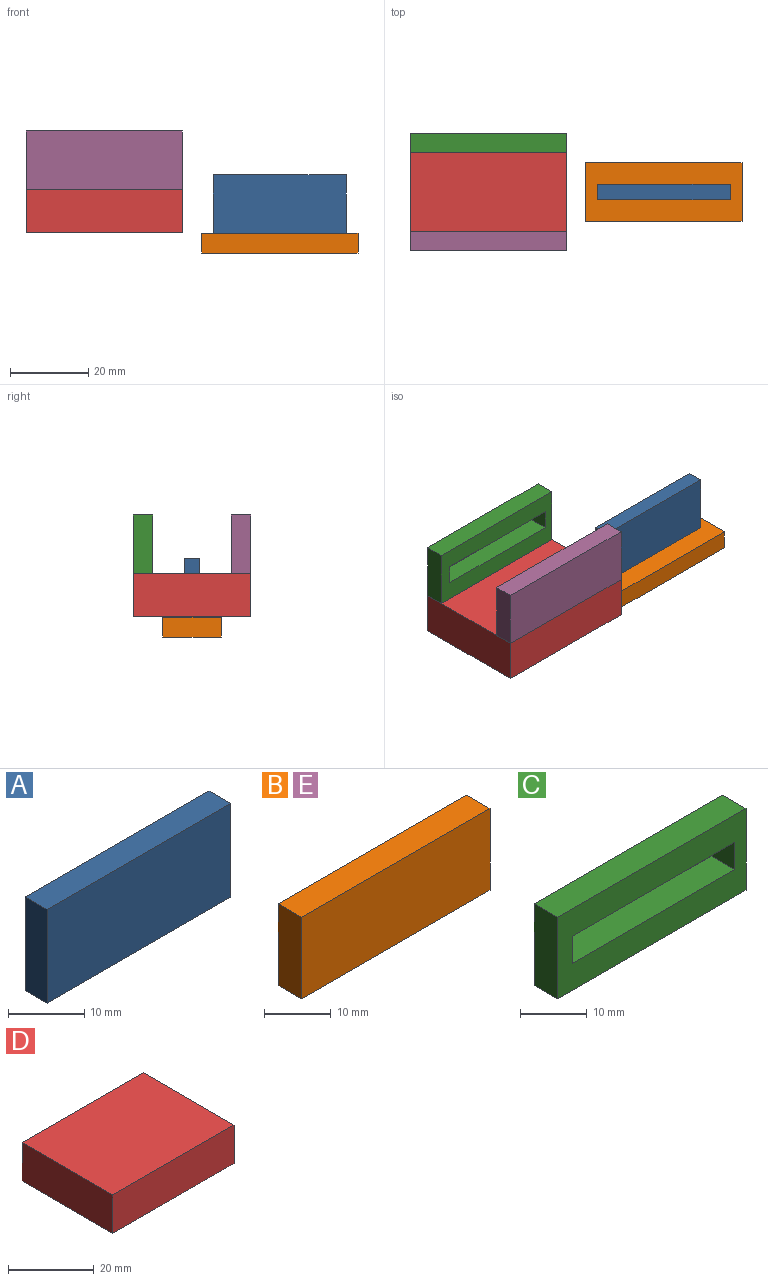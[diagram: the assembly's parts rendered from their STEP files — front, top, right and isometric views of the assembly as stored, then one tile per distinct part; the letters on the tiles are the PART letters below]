
ASSEMBLY  parts=5 mates=3
PART A: 6 faces, bbox 34x4x15 mm
  f0: plane 15x4mm, normal (-1,0,0), area 60mm2, adj f1,f3,f4,f5
  f1: plane 34x4mm, normal (0,0,-1), area 136mm2, adj f0,f2,f4,f5
  f2: plane 15x4mm, normal (1,0,0), area 60mm2, adj f1,f3,f4,f5
  f3: plane 34x4mm, normal (0,0,1), area 136mm2, adj f0,f2,f4,f5
  f4: plane 34x15mm, normal (0,-1,0), area 510mm2, adj f0,f1,f2,f3
  f5: plane 34x15mm, normal (0,1,0), area 510mm2, adj f0,f1,f2,f3
PART B: 6 faces, bbox 40x5x15 mm
  f0: plane 40x5mm, normal (0,0,1), area 200mm2, adj f1,f3,f4,f5
  f1: plane 15x5mm, normal (-1,0,0), area 75mm2, adj f0,f2,f4,f5
  f2: plane 40x5mm, normal (0,0,-1), area 200mm2, adj f1,f3,f4,f5
  f3: plane 15x5mm, normal (1,0,0), area 75mm2, adj f0,f2,f4,f5
  f4: plane 40x15mm, normal (0,-1,0), area 600mm2, adj f0,f1,f2,f3
  f5: plane 40x15mm, normal (0,1,0), area 600mm2, adj f0,f1,f2,f3
PART C: 10 faces, bbox 40x5x15 mm
  f0: plane 40x5mm, normal (0,0,1), area 200mm2, adj f1,f7,f8,f9
  f1: plane 15x5mm, normal (-1,0,0), area 75mm2, adj f0,f2,f8,f9
  f2: plane 40x5mm, normal (0,0,-1), area 200mm2, adj f1,f7,f8,f9
  f3: plane 5x5mm, normal (-1,0,0), area 25mm2, adj f4,f6,f8,f9
  f4: plane 34.5x5mm, normal (0,0,1), area 172.5mm2, adj f3,f5,f8,f9
  f5: plane 5x5mm, normal (1,0,0), area 25mm2, adj f4,f6,f8,f9
  f6: plane 34.5x5mm, normal (0,0,-1), area 172.5mm2, adj f3,f5,f8,f9
  f7: plane 15x5mm, normal (1,0,0), area 75mm2, adj f0,f2,f8,f9
  f8: plane 40x15mm, normal (0,-1,0), area 427.5mm2, adj f0,f1,f2,f3,f4,f5,f6,f7
  f9: plane 40x15mm, normal (0,1,0), area 427.5mm2, adj f0,f1,f2,f3,f4,f5,f6,f7
PART D: 6 faces, bbox 40x30x11 mm
  f0: plane 40x30mm, normal (0,0,1), area 1200mm2, adj f1,f3,f4,f5
  f1: plane 30x11mm, normal (-1,0,0), area 330mm2, adj f0,f2,f4,f5
  f2: plane 40x30mm, normal (0,0,-1), area 1200mm2, adj f1,f3,f4,f5
  f3: plane 30x11mm, normal (1,0,0), area 330mm2, adj f0,f2,f4,f5
  f4: plane 40x11mm, normal (0,-1,0), area 440mm2, adj f0,f1,f2,f3
  f5: plane 40x11mm, normal (0,1,0), area 440mm2, adj f0,f1,f2,f3
PART E: same geometry as B
PLACE A rot(axis=(0,0,-1),180deg) t=(88.53,-1.48,-5.12)mm
PLACE B rot(axis=(0,0.71,0.71),180deg) t=(91.42,-3.92,-12.17)mm
PLACE C t=(35.09,15.52,7.77)mm
PLACE D rot(axis=(0,0.24,0.97),0deg) t=(14.75,15.52,-0.97)mm
PLACE E t=(22.99,-9.48,2.09)mm
MATE fastened D.f0 <-> C.f2  axis (0,0,1) through (34.75,13.02,-0.97)mm
MATE fastened A.f1 <-> B.f5  axis (0,0,-1) through (79.65,0.52,-12.17)mm
MATE fastened D.f0 <-> E.f2  axis (0,0,1) through (34.75,-11.98,-0.97)mm
